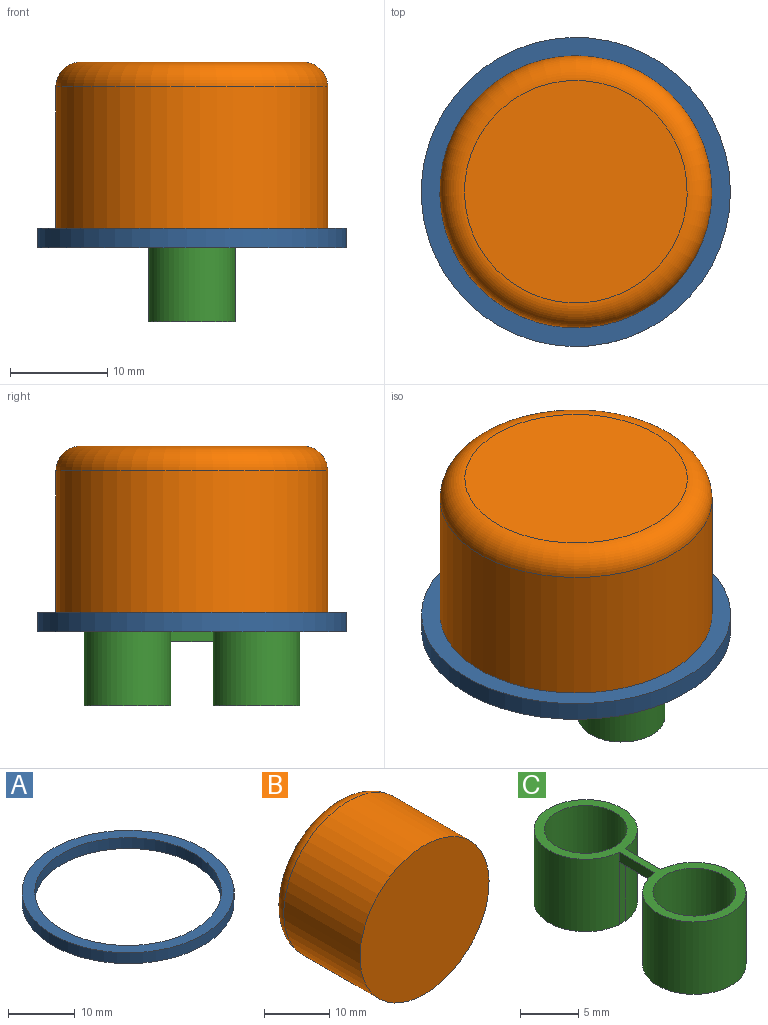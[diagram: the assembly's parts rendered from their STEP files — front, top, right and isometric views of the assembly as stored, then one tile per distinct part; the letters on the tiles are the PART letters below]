
ASSEMBLY  parts=3 mates=2
PART A: 4 faces, bbox 31.8x31.8x2 mm
  f0: cylinder r=13.97mm len=27.94mm, axis (0,0,-1), area 173.9mm2, adj f2,f3
  f1: cylinder r=15.88mm len=31.75mm, axis (0,0,-1), area 197.6mm2, adj f2,f3
  f2: plane 31.75x31.75mm, normal (0,0,1), area 178.6mm2, adj f0,f1
  f3: plane 31.75x31.75mm, normal (0,0,-1), area 178.6mm2, adj f0,f1
PART B: 4 faces, bbox 30.2x19.1x30.2 mm
  f0: cylinder r=13.97mm len=27.94mm, axis (0,-1,0), area 1449.2mm2, adj f2,f3
  f1: plane 22.86x22.86mm, normal (0,1,0), area 410.4mm2, adj f3
  f2: plane 27.94x27.94mm, normal (0,-1,0), area 613.1mm2, adj f0
  f3: torus R=11.43mm, axis (0,-1,0), area 327.1mm2, adj f0,f1
PART C: 12 faces, bbox 8.9x22.1x7.6 mm
  f0: plane 8.89x8.88mm, normal (0,0,-1), area 22.3mm2, adj f1,f5,f9
  f1: cylinder r=4.45mm len=8.89mm, axis (0,0,-1), area 207.4mm2, adj f0,f2,f4,f7,f9
  f2: plane 4.35x1.04mm, normal (-1,0,0), area 4.5mm2, adj f1,f3,f7,f11
  f3: cylinder r=4.45mm len=8.89mm, axis (0,0,-1), area 207.4mm2, adj f2,f4,f7,f8,f10
  f4: plane 4.35x1.04mm, normal (1,0,0), area 4.5mm2, adj f1,f3,f7,f11
  f5: cylinder r=3.56mm len=7.62mm, axis (0,0,-1), area 170.3mm2, adj f0,f7
  f6: cylinder r=3.56mm len=7.62mm, axis (0,0,-1), area 170.3mm2, adj f7,f8
  f7: plane 22.1x8.89mm, normal (0,0,1), area 47.8mm2, adj f1,f2,f3,f4,f5,f6
  f8: plane 8.89x8.88mm, normal (0,0,-1), area 22.3mm2, adj f3,f6,f10
  f9: plane 6.58x0.71mm, normal (0,-1,0), area 4.7mm2, adj f0,f1,f11
  f10: plane 6.58x0.71mm, normal (0,1,0), area 4.7mm2, adj f3,f8,f11
  f11: plane 4.35x0.71mm, normal (0,0,-1), area 3.1mm2, adj f2,f4,f9,f10
PLACE A t=(-18.16,-6.86,31.99)mm
PLACE B rot(axis=(1,0,0),90deg) t=(-20.59,-6.86,31.99)mm
PLACE C t=(-18.16,-6.86,24.37)mm
MATE fastened B.f0 <-> A.f0  axis (0,0,-1) through (-18.16,-6.86,31.99)mm
MATE fastened C.f7 <-> B.f0  axis (0,0,1) through (-18.16,-6.86,31.99)mm
